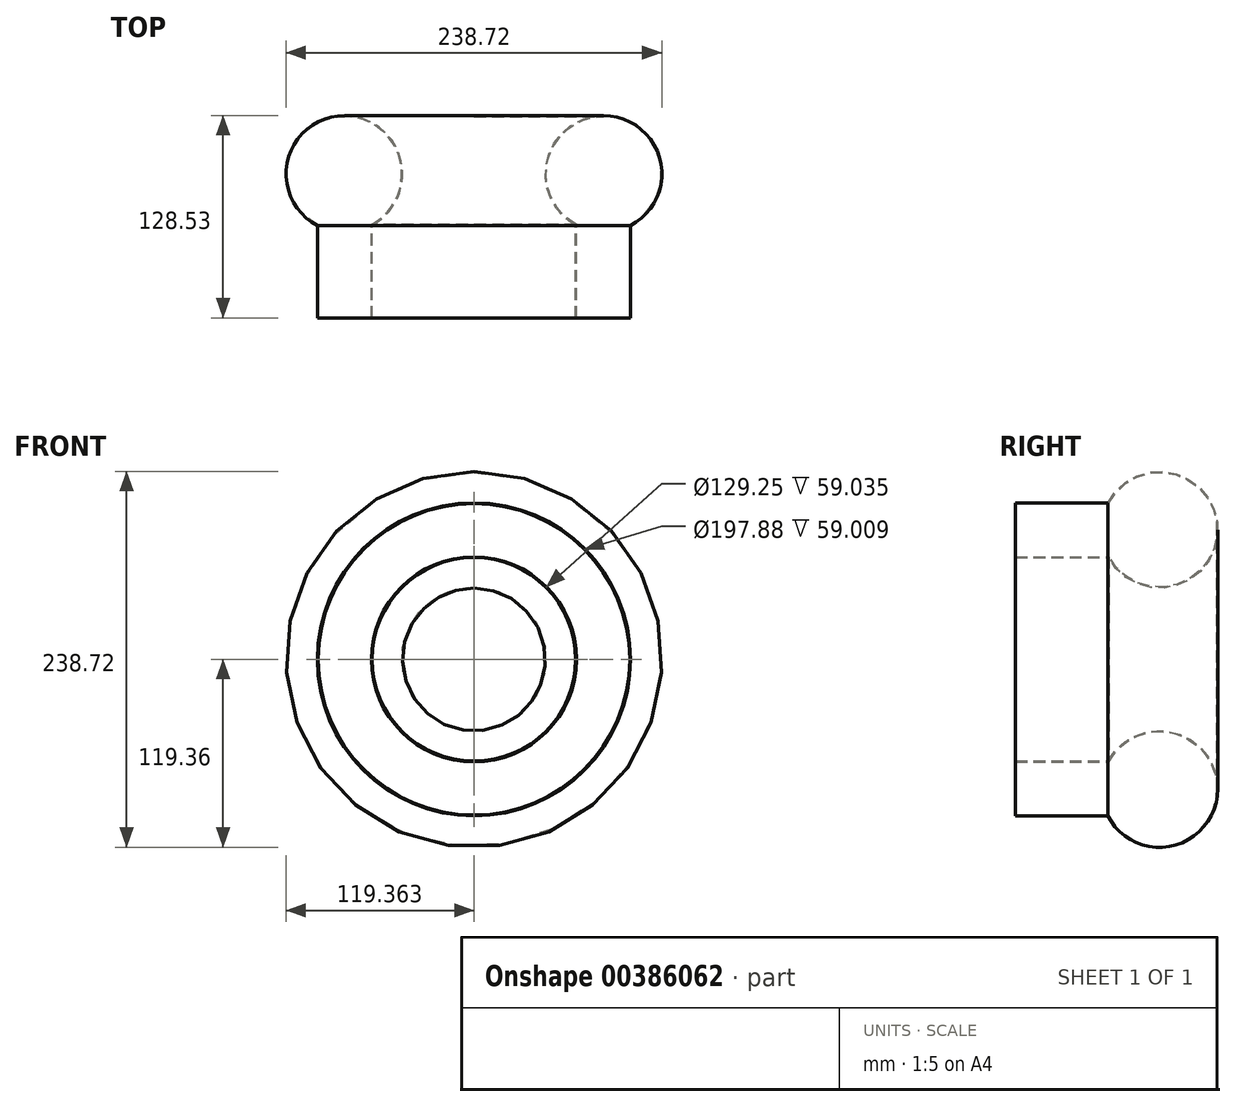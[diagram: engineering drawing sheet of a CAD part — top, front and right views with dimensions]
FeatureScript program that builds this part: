
annotation { "Feature Type Name" : "Feature", "Feature Type Description" : "" }
export const myFeature = defineFeature(function(context is Context, id is Id, definition is map)
    precondition{}
    {
        {
            var Q0;
            Q0=qCreatedBy(makeId("Top.planeOp"),FACE);
            var sketch = newSketch(context, id + "F0", { "sketchPlane" : qUnion([Q0])});
            skCircle(sketch, "E0", {"center": v(0.8, 30.87) * mm, "radius": 37 * mm});
            skCircle(sketch, "E1", {"center": v(-12.7, 51.4) * mm, "radius": 4.84 * mm});
            skCircle(sketch, "E2", {"center": v(13.17, 51.4) * mm, "radius": 5.46 * mm});
            skLineSegment(sketch, "E3", {"start": v(5.76, -5.8) * mm, "end": v(5.76, -50.69) * mm});
            skLineSegment(sketch, "E4.bottom", {"start": v(-15.47, 40.64) * mm, "end": v(18, 40.64) * mm});
            skLineSegment(sketch, "E4.top", {"start": v(-15.47, 9.7) * mm, "end": v(18, 9.7) * mm});
            skLineSegment(sketch, "E4.left", {"start": v(-15.47, 40.64) * mm, "end": v(-15.47, 9.7) * mm});
            skLineSegment(sketch, "E4.right", {"start": v(18, 40.64) * mm, "end": v(18, 9.7) * mm});
            skLineSegment(sketch, "E5", {"start": v(-5.09, -5.67) * mm, "end": v(-5.09, -50.48) * mm});
            skLineSegment(sketch, "E6", {"start": v(-5.09, -50.48) * mm, "end": v(8.44, -50.69) * mm});
            skLineSegment(sketch, "E7", {"start": v(-10.6, -4.34) * mm, "end": v(-10.6, -50.48) * mm});
            skLineSegment(sketch, "E8", {"start": v(-10.6, -50.48) * mm, "end": v(-10.6, -56.13) * mm});
            skLineSegment(sketch, "E9", {"start": v(-10.6, -56.13) * mm, "end": v(12.1, -56.13) * mm});
            skLineSegment(sketch, "E10", {"start": v(12.1, -56.13) * mm, "end": v(12.1, -4.37) * mm});
            skLineSegment(sketch, "E11", {"start": v(-16.93, -1.62) * mm, "end": v(-16.93, -58.9) * mm});
            skLineSegment(sketch, "E12", {"start": v(-16.93, -60.65) * mm, "end": v(17.9, -60.65) * mm});
            skLineSegment(sketch, "E13", {"start": v(17.9, -60.65) * mm, "end": v(17.9, -1.95) * mm});
            skLineSegment(sketch, "E14", {"start": v(17.9, -1.95) * mm, "end": v(-16.93, -1.62) * mm});
            skLineSegment(sketch, "E15", {"start": v(-16.93, -58.9) * mm, "end": v(-16.93, -60.65) * mm});
            skLineSegment(sketch, "E16", {"start": v(-56.8, 60.89) * mm, "end": v(-16.93, -60.65) * mm});
            skLineSegment(sketch, "E17", {"start": v(-81.56, 53.01) * mm, "end": v(-81.56, -57.8) * mm});
            skSolve(sketch);
        }
        {
            var Q0;
            Q0=makeQuery(id+"F0.imprint","IMPRINT",FACE,{"disambiguationData":[TD([[makeQuery(id+"F0.imprint","IMPRINT",EDGE,{"derivedFrom":sQuery(id+"F0.wireOp",EDGE,"E1")}),1.0]])]});
            var Q1;
            Q1=makeQuery(id+"F0.imprint","IMPRINT",FACE,{"disambiguationData":[TD([[makeQuery(id+"F0.imprint","IMPRINT",EDGE,{"derivedFrom":sQuery(id+"F0.wireOp",EDGE,"E2")}),1.0]])]});
            var Q2;
            Q2=makeQuery(id+"F0.imprint","IMPRINT",FACE,{"disambiguationData":[TD([[makeQuery(id+"F0.imprint","IMPRINT",EDGE,{"derivedFrom":sQuery(id+"F0.wireOp",EDGE,"E4.bottom")}),-1.0]])]});
            var Q3;
            {var subQ4=sQuery(id+"F0.wireOp",EDGE,"E7");Q3=makeQuery(id+"F0.imprint","IMPRINT",FACE,{"disambiguationData":[TD([[makeQuery(id+"F0.imprint","IMPRINT",EDGE,{"derivedFrom":subQ4}),-1.0]])]});}
            var Q4;
            {var subQ3=sQuery(id+"F0.wireOp",EDGE,"E5");Q4=makeQuery(id+"F0.imprint","IMPRINT",FACE,{"disambiguationData":[TD([[makeQuery(id+"F0.imprint","IMPRINT",EDGE,{"derivedFrom":subQ3}),1.0]])]});}
            var Q5;
            {var subQ0=sQuery(id+"F0.wireOp",EDGE,"E5");Q5=makeQuery(id+"F0.imprint","IMPRINT",FACE,{"disambiguationData":[TD([[makeQuery(id+"F0.imprint","IMPRINT",EDGE,{"derivedFrom":subQ0}),-1.0]])]});}
            var Q6;
            {var subQ5=sQuery(id+"F0.wireOp",EDGE,"E14");Q6=makeQuery(id+"F0.imprint","IMPRINT",FACE,{"disambiguationData":[TD([[makeQuery(id+"F0.imprint","IMPRINT",EDGE,{"derivedFrom":subQ5}),1.0]])]});}
            var Q7;
            Q7=makeQuery(id+"F0.imprint","IMPRINT",FACE,{"disambiguationData":[TD([[makeQuery(id+"F0.imprint","IMPRINT",EDGE,{"derivedFrom":sQuery(id+"F0.wireOp",EDGE,"E1")}),-1.0]])]});
            var Q8;
            Q8=sQuery(id+"F0.wireOp",EDGE,"E17");
            revolve(context, id + "F1", {"entities" : qUnion([Q0, Q1, Q2, Q3, Q4, Q5, Q6, Q7]), "axis" : qUnion([Q8]), "revolveType" : RevolveType.FULL});
        }
        {
            var Q0;
            Q0=makeQuery(id+"F1.opRevolve","SWEPT_FACE",FACE,{"disambiguationData":[OSD([sQuery(id+"F0.wireOp",EDGE,"E12")])]});
            shell(context, id + "F2", {"entities" : qUnion([Q0]), "thickness" : 0.5 * mm});
        }
    });
